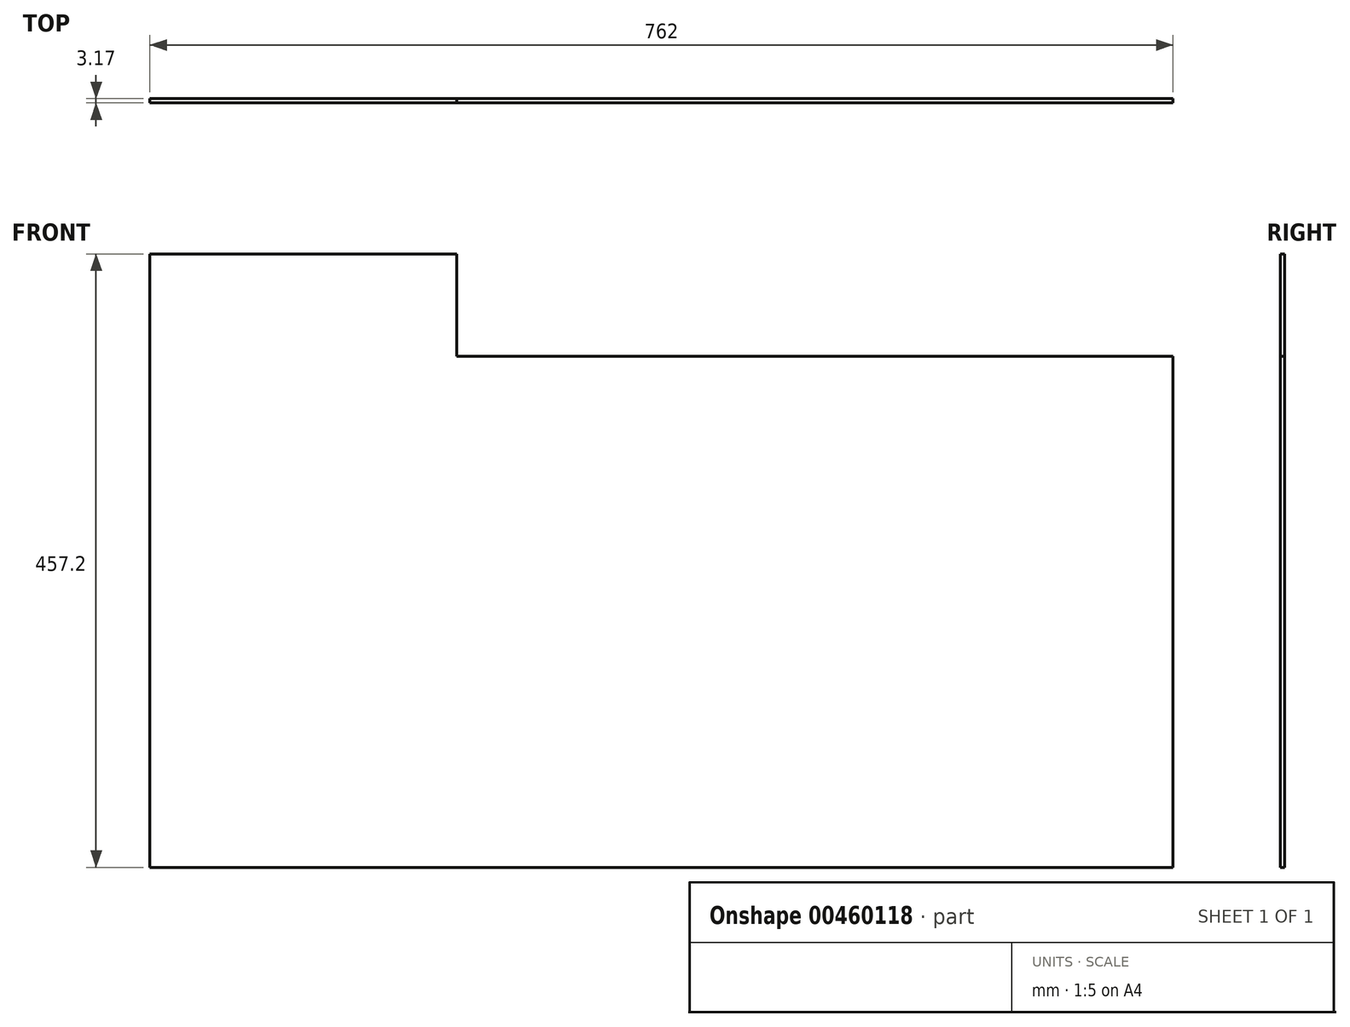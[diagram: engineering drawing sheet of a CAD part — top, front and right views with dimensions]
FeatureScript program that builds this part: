
annotation { "Feature Type Name" : "Feature", "Feature Type Description" : "" }
export const myFeature = defineFeature(function(context is Context, id is Id, definition is map)
    precondition{}
    {
        {
            var Q0;
            Q0=qCreatedBy(makeId("Front.planeOp"),FACE);
            var sketch = newSketch(context, id + "F0", { "sketchPlane" : qUnion([Q0])});
            skLineSegment(sketch, "E0", {"start": v(-277.58, 237.1) * mm, "end": v(-48.98, 237.1) * mm});
            skLineSegment(sketch, "E1", {"start": v(484.42, 160.9) * mm, "end": v(484.42, -220.1) * mm});
            skLineSegment(sketch, "E2", {"start": v(-277.58, 237.1) * mm, "end": v(-277.58, -220.1) * mm});
            skLineSegment(sketch, "E3", {"start": v(-277.58, -220.1) * mm, "end": v(484.42, -220.1) * mm});
            skLineSegment(sketch, "E4", {"start": v(-48.98, 237.1) * mm, "end": v(-48.98, 160.9) * mm});
            skLineSegment(sketch, "E5", {"start": v(-48.98, 160.9) * mm, "end": v(484.42, 160.9) * mm});
            skSolve(sketch);
        }
        {
            var Q0;
            Q0=makeQuery(id+"F0.imprint","IMPRINT",FACE,{"disambiguationData":[TD([[makeQuery(id+"F0.imprint","IMPRINT",EDGE,{"derivedFrom":sQuery(id+"F0.wireOp",EDGE,"E0")}),-1.0]])]});
            extrude(context, id + "F1", {"entities" : qUnion([Q0]), "depth" : 3.17 * mm});
        }
    });
